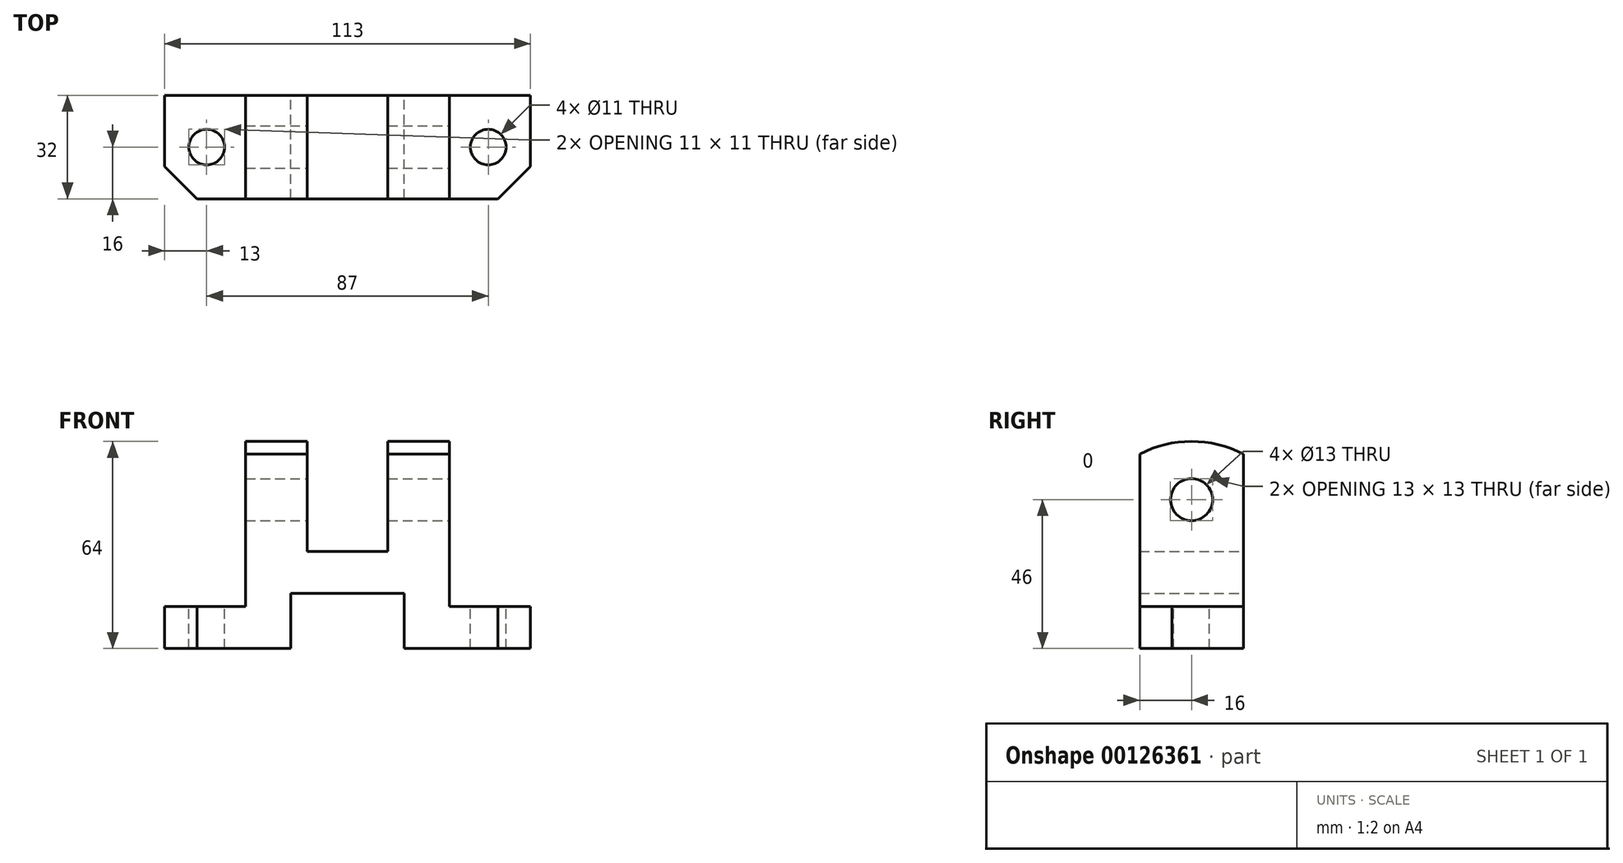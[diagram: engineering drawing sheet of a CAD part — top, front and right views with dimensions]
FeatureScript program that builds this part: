
annotation { "Feature Type Name" : "Feature", "Feature Type Description" : "" }
export const myFeature = defineFeature(function(context is Context, id is Id, definition is map)
    precondition{}
    {
        {
            var Q0;
            Q0=qCreatedBy(makeId("Front.planeOp"),FACE);
            var sketch = newSketch(context, id + "F0", { "sketchPlane" : qUnion([Q0])});
            skLineSegment(sketch, "E0", {"start": v(0, 0) * mm, "end": v(0, 13) * mm});
            skLineSegment(sketch, "E1", {"start": v(0, 13) * mm, "end": v(25, 13) * mm});
            skLineSegment(sketch, "E2", {"start": v(25, 13) * mm, "end": v(25, 64) * mm});
            skLineSegment(sketch, "E3", {"start": v(25, 64) * mm, "end": v(44, 64) * mm});
            skLineSegment(sketch, "E4", {"start": v(44, 64) * mm, "end": v(44, 30) * mm});
            skLineSegment(sketch, "E5", {"start": v(44, 30) * mm, "end": v(69, 30) * mm});
            skLineSegment(sketch, "E6", {"start": v(69, 30) * mm, "end": v(69, 64) * mm});
            skLineSegment(sketch, "E7", {"start": v(69, 64) * mm, "end": v(88, 64) * mm});
            skLineSegment(sketch, "E8", {"start": v(88, 64) * mm, "end": v(88, 13) * mm});
            skLineSegment(sketch, "E9", {"start": v(88, 13) * mm, "end": v(113, 13) * mm});
            skLineSegment(sketch, "E10", {"start": v(113, 13) * mm, "end": v(113, 0) * mm});
            skLineSegment(sketch, "E11", {"start": v(113, 0) * mm, "end": v(74, 0) * mm});
            skLineSegment(sketch, "E12", {"start": v(74, 0) * mm, "end": v(74, 17) * mm});
            skLineSegment(sketch, "E13", {"start": v(74, 17) * mm, "end": v(39, 17) * mm});
            skLineSegment(sketch, "E14", {"start": v(39, 17) * mm, "end": v(39, 0) * mm});
            skLineSegment(sketch, "E15", {"start": v(39, 0) * mm, "end": v(0, 0) * mm});
            skSolve(sketch);
        }
        {
            var Q0;
            Q0 = qSketchRegion(id + "F0", true);
            extrude(context, id + "F1", {"entities" : qUnion([Q0]), "endBound" : BoundingType.SYMMETRIC, "depth" : 32 * mm});
        }
        {
            var Q0;
            Q0=makeQuery(id+"F1.opExtrude","SWEPT_FACE",FACE,{"disambiguationData":[OSD([sQuery(id+"F0.wireOp",EDGE,"E1")])]});
            var sketch = newSketch(context, id + "F2", { "sketchPlane" : qUnion([Q0])});
            skLineSegment(sketch, "E16", {"start": v(0, -6) * mm, "end": v(10, -16) * mm});
            skSolve(sketch);
        }
        {
            var Q0;
            Q0 = qSketchRegion(id + "F2", true);
            var Q1;
            {var subQ0=sQuery(id+"F2.wireOp",EDGE,"E16");Q1=makeQuery(id+"F2.imprint","IMPRINT",FACE,{"disambiguationData":[TD([[makeQuery(id+"F2.imprint","IMPRINT",EDGE,{"derivedFrom":subQ0}),-1.0]])]});}
            extrude(context, id + "F3", {"entities" : qUnion([Q0, Q1]), "operationType" : NewBodyOperationType.REMOVE, "endBound" : BoundingType.THROUGH_ALL, "oppositeDirection" : true, "depth" : 25 * mm});
        }
        {
            var Q0;
            Q0=makeQuery(id+"F1.opExtrude","SWEPT_FACE",FACE,{"disambiguationData":[OSD([sQuery(id+"F0.wireOp",EDGE,"E9")])]});
            var sketch = newSketch(context, id + "F4", { "sketchPlane" : qUnion([Q0])});
            skLineSegment(sketch, "E17", {"start": v(103, -16) * mm, "end": v(113, -6) * mm});
            skSolve(sketch);
        }
        {
            var Q0;
            Q0 = qSketchRegion(id + "F4", true);
            var Q1;
            {var subQ0=sQuery(id+"F4.wireOp",EDGE,"E17");Q1=makeQuery(id+"F4.imprint","IMPRINT",FACE,{"disambiguationData":[TD([[makeQuery(id+"F4.imprint","IMPRINT",EDGE,{"derivedFrom":subQ0}),-1.0]])]});}
            extrude(context, id + "F5", {"entities" : qUnion([Q0, Q1]), "operationType" : NewBodyOperationType.REMOVE, "endBound" : BoundingType.THROUGH_ALL, "oppositeDirection" : true, "depth" : 25 * mm});
        }
        {
            var Q0;
            Q0=makeQuery(id+"F1.opExtrude","SWEPT_FACE",FACE,{"disambiguationData":[OSD([sQuery(id+"F0.wireOp",EDGE,"E8")])]});
            var sketch = newSketch(context, id + "F6", { "sketchPlane" : qUnion([Q0])});
            skLineSegment(sketch, "E18", {"start": v(0, 79.32) * mm, "end": v(0, -9.3) * mm, "construction": true});
            skPoint(sketch, "E18.endSnap0", {"position": v(0, 13) * mm});
            skCircle(sketch, "E19", {"center": v(0, 46) * mm, "radius": 6.5 * mm});
            skSolve(sketch);
        }
        {
            var Q0;
            Q0 = qSketchRegion(id + "F6", true);
            extrude(context, id + "F7", {"entities" : qUnion([Q0]), "operationType" : NewBodyOperationType.REMOVE, "endBound" : BoundingType.THROUGH_ALL, "oppositeDirection" : true, "depth" : 25 * mm});
        }
        {
            var Q0;
            Q0=makeQuery(id+"F1.opExtrude","SWEPT_FACE",FACE,{"disambiguationData":[OSD([sQuery(id+"F0.wireOp",EDGE,"E9")])]});
            var sketch = newSketch(context, id + "F8", { "sketchPlane" : qUnion([Q0])});
            skCircle(sketch, "E20", {"center": v(100, 0) * mm, "radius": 5.5 * mm});
            skCircle(sketch, "E21", {"center": v(13, 0) * mm, "radius": 5.5 * mm});
            skSolve(sketch);
        }
        {
            var Q0;
            Q0=makeQuery(id+"F8.imprint","IMPRINT",FACE,{"disambiguationData":[TD([[makeQuery(id+"F8.imprint","IMPRINT",EDGE,{"derivedFrom":sQuery(id+"F8.wireOp",EDGE,"E20")}),1.0]])]});
            var Q1;
            Q1=makeQuery(id+"F8.imprint","IMPRINT",FACE,{"disambiguationData":[TD([[makeQuery(id+"F8.imprint","IMPRINT",EDGE,{"derivedFrom":sQuery(id+"F8.wireOp",EDGE,"E21")}),1.0]])]});
            extrude(context, id + "F9", {"entities" : qUnion([Q0, Q1]), "operationType" : NewBodyOperationType.REMOVE, "endBound" : BoundingType.THROUGH_ALL, "oppositeDirection" : true, "depth" : 25 * mm});
        }
        {
            var Q0;
            Q0=makeQuery(id+"F1.opExtrude","SWEPT_FACE",FACE,{"disambiguationData":[OSD([sQuery(id+"F0.wireOp",EDGE,"E8")])]});
            var sketch = newSketch(context, id + "F10", { "sketchPlane" : qUnion([Q0])});
            skArc(sketch, "E22", {"start": v(16, 60.13) * mm, "mid": v(0, 64) * mm, "end": v(-16, 60.13) * mm});
            skSolve(sketch);
        }
        {
            var Q0;
            Q0 = qSketchRegion(id + "F10", true);
            var Q1;
            {var subQ0=sQuery(id+"F10.wireOp",EDGE,"E22");var subQ1=sQuery(id+"F0.wireOp",EDGE,"E8");var subQ2=makeQuery(id+"F1.opExtrude","CAP_EDGE",EDGE,{"disambiguationData":[OSD([subQ1])],"isStart":false});var subQ3=makeQuery(id+"F10.imprint","INTERSECT",VERTEX,{"derivedFrom":[subQ2,subQ0]});Q1=makeQuery(id+"F10.imprint","IMPRINT",FACE,{"disambiguationData":[TD([[makeQuery(id+"F10.imprint","IMPRINT",EDGE,{"disambiguationData":[TD([[subQ3,1.0]])],"derivedFrom":subQ0}),-1.0]])]});}
            var Q2;
            {var subQ0=sQuery(id+"F10.wireOp",EDGE,"E22");var subQ1=sQuery(id+"F0.wireOp",EDGE,"E8");var subQ2=makeQuery(id+"F1.opExtrude","CAP_EDGE",EDGE,{"disambiguationData":[OSD([subQ1])],"isStart":true});var subQ3=makeQuery(id+"F10.imprint","INTERSECT",VERTEX,{"derivedFrom":[subQ2,subQ0]});Q2=makeQuery(id+"F10.imprint","IMPRINT",FACE,{"disambiguationData":[TD([[makeQuery(id+"F10.imprint","IMPRINT",EDGE,{"disambiguationData":[TD([[subQ3,-1.0]])],"derivedFrom":subQ0}),-1.0]])]});}
            extrude(context, id + "F11", {"entities" : qUnion([Q0, Q1, Q2]), "operationType" : NewBodyOperationType.REMOVE, "endBound" : BoundingType.THROUGH_ALL, "oppositeDirection" : true, "depth" : 25 * mm});
        }
    });
